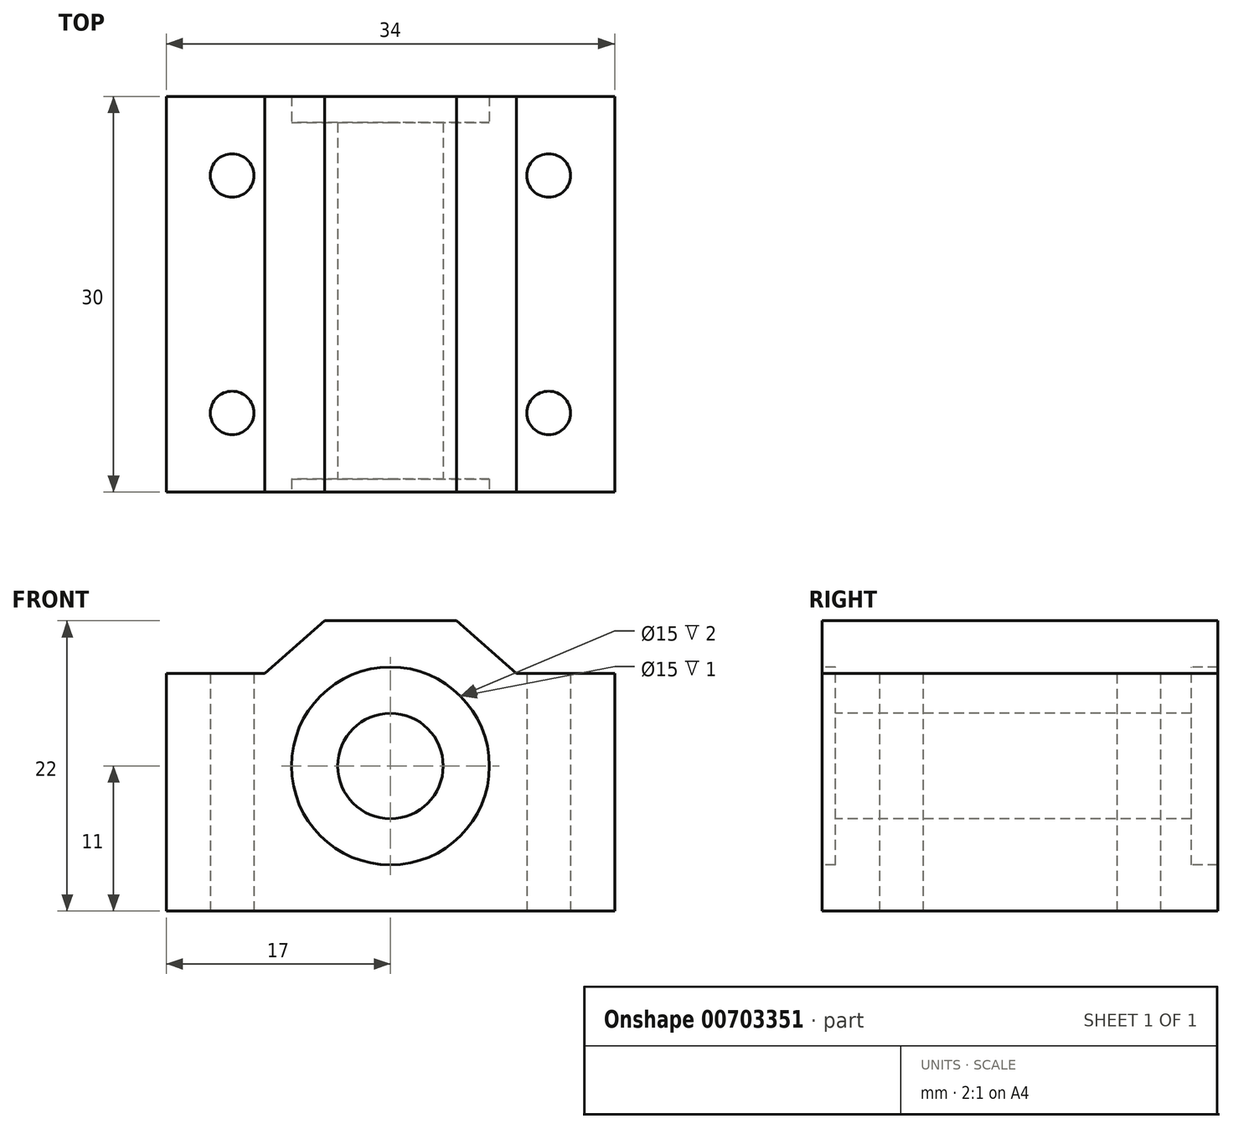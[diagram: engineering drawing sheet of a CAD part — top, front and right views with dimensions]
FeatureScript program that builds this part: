
annotation { "Feature Type Name" : "Feature", "Feature Type Description" : "" }
export const myFeature = defineFeature(function(context is Context, id is Id, definition is map)
    precondition{}
    {
        {
            var Q0;
            Q0=qCreatedBy(makeId("Front.planeOp"),FACE);
            var sketch = newSketch(context, id + "F0", { "sketchPlane" : qUnion([Q0])});
            skLineSegment(sketch, "E0", {"start": v(-44, 0) * mm, "end": v(-10, 0) * mm});
            skLineSegment(sketch, "E1", {"start": v(-10, 0) * mm, "end": v(-10, 18) * mm});
            skLineSegment(sketch, "E2", {"start": v(-10, 18) * mm, "end": v(-17.46, 18) * mm});
            skLineSegment(sketch, "E3", {"start": v(-17.46, 18) * mm, "end": v(-22, 22) * mm});
            skLineSegment(sketch, "E4", {"start": v(-22, 22) * mm, "end": v(-32, 22) * mm});
            skLineSegment(sketch, "E5", {"start": v(-32, 22) * mm, "end": v(-36.54, 18) * mm});
            skLineSegment(sketch, "E6", {"start": v(-36.54, 18) * mm, "end": v(-44, 18) * mm});
            skLineSegment(sketch, "E7", {"start": v(-44, 18) * mm, "end": v(-44, 0) * mm});
            skCircle(sketch, "E8", {"center": v(-27, 11) * mm, "radius": 4 * mm});
            skCircle(sketch, "E9", {"center": v(-27, 11) * mm, "radius": 7.5 * mm});
            skSolve(sketch);
        }
        {
            var Q0;
            Q0=makeQuery(id+"F0.imprint","IMPRINT",FACE,{"disambiguationData":[TD([[makeQuery(id+"F0.imprint","IMPRINT",EDGE,{"derivedFrom":sQuery(id+"F0.wireOp",EDGE,"E0")}),1.0]])]});
            extrude(context, id + "F1", {"entities" : qUnion([Q0]), "oppositeDirection" : true, "depth" : 30 * mm, "offsetDistance" : 25 * mm});
        }
        {
            var Q0;
            Q0=makeQuery(id+"F0.imprint","IMPRINT",FACE,{"disambiguationData":[TD([[makeQuery(id+"F0.imprint","IMPRINT",EDGE,{"derivedFrom":sQuery(id+"F0.wireOp",EDGE,"E8")}),-1.0]])]});
            extrude(context, id + "F2", {"entities" : qUnion([Q0]), "operationType" : NewBodyOperationType.ADD, "oppositeDirection" : true, "depth" : 28 * mm, "offsetDistance" : 25 * mm, "hasSecondDirection" : true, "secondDirectionOppositeDirection" : true, "secondDirectionDepth" : 1 * mm});
        }
        {
            var Q0;
            Q0=makeQuery(id+"F1.opExtrude","SWEPT_FACE",FACE,{"disambiguationData":[OSD([sQuery(id+"F0.wireOp",EDGE,"E0")])]});
            var sketch = newSketch(context, id + "F3", { "sketchPlane" : qUnion([Q0])});
            skLineSegment(sketch, "E10.bottom", {"start": v(-39, -6) * mm, "end": v(-15, -6) * mm, "construction": true});
            skLineSegment(sketch, "E10.top", {"start": v(-39, -24) * mm, "end": v(-15, -24) * mm, "construction": true});
            skLineSegment(sketch, "E10.left", {"start": v(-39, -6) * mm, "end": v(-39, -24) * mm, "construction": true});
            skLineSegment(sketch, "E10.right", {"start": v(-15, -6) * mm, "end": v(-15, -24) * mm, "construction": true});
            skCircle(sketch, "E11", {"center": v(-39, -6) * mm, "radius": 1.65 * mm});
            skCircle(sketch, "E12", {"center": v(-39, -6) * mm, "radius": 2 * mm});
            skCircle(sketch, "E13.0.1.0", {"center": v(-39, -24) * mm, "radius": 1.65 * mm});
            skCircle(sketch, "E13.0.1.1", {"center": v(-39, -24) * mm, "radius": 2 * mm});
            skCircle(sketch, "E13.1.0.0", {"center": v(-15, -6) * mm, "radius": 1.65 * mm});
            skCircle(sketch, "E13.1.0.1", {"center": v(-15, -6) * mm, "radius": 2 * mm});
            skCircle(sketch, "E13.1.1.0", {"center": v(-15, -24) * mm, "radius": 1.65 * mm});
            skCircle(sketch, "E13.1.1.1", {"center": v(-15, -24) * mm, "radius": 2 * mm});
            skSolve(sketch);
        }
        {
            var Q0;
            Q0=makeQuery(id+"F3.imprint","IMPRINT",FACE,{"disambiguationData":[TD([[makeQuery(id+"F3.imprint","IMPRINT",EDGE,{"derivedFrom":sQuery(id+"F3.wireOp",EDGE,"E11")}),1.0]])]});
            var Q1;
            Q1=makeQuery(id+"F3.imprint","IMPRINT",FACE,{"disambiguationData":[TD([[makeQuery(id+"F3.imprint","IMPRINT",EDGE,{"derivedFrom":sQuery(id+"F3.wireOp",EDGE,"E13.1.0.0")}),1.0]])]});
            var Q2;
            Q2=makeQuery(id+"F3.imprint","IMPRINT",FACE,{"disambiguationData":[TD([[makeQuery(id+"F3.imprint","IMPRINT",EDGE,{"derivedFrom":sQuery(id+"F3.wireOp",EDGE,"E13.1.1.0")}),1.0]])]});
            var Q3;
            Q3=makeQuery(id+"F3.imprint","IMPRINT",FACE,{"disambiguationData":[TD([[makeQuery(id+"F3.imprint","IMPRINT",EDGE,{"derivedFrom":sQuery(id+"F3.wireOp",EDGE,"E13.0.1.0")}),1.0]])]});
            extrude(context, id + "F4", {"entities" : qUnion([Q0, Q1, Q2, Q3]), "operationType" : NewBodyOperationType.REMOVE, "oppositeDirection" : true, "depth" : 25 * mm, "offsetDistance" : 25 * mm});
        }
    });
